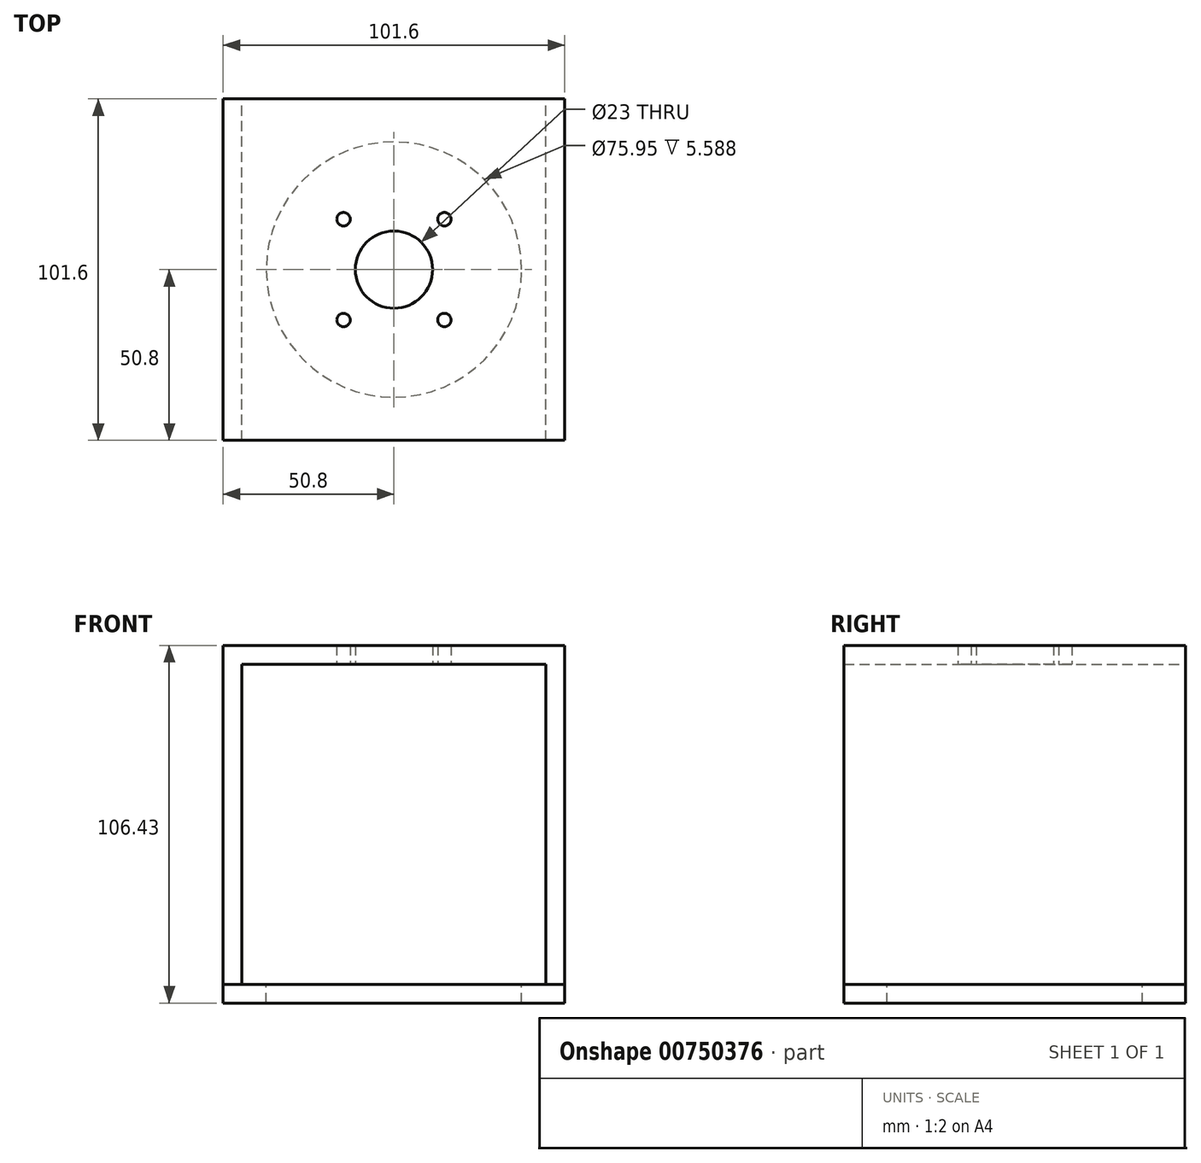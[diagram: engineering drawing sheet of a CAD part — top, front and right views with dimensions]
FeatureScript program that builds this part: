
annotation { "Feature Type Name" : "Feature", "Feature Type Description" : "" }
export const myFeature = defineFeature(function(context is Context, id is Id, definition is map)
    precondition{}
    {
        {
            var Q0;
            Q0=qCreatedBy(makeId("Top.planeOp"),FACE);
            var sketch = newSketch(context, id + "F0", { "sketchPlane" : qUnion([Q0])});
            skLineSegment(sketch, "E0.bottom", {"start": v(50.8, -50.8) * mm, "end": v(-50.8, -50.8) * mm});
            skLineSegment(sketch, "E0.top", {"start": v(50.8, 50.8) * mm, "end": v(-50.8, 50.8) * mm});
            skLineSegment(sketch, "E0.left", {"start": v(50.8, -50.8) * mm, "end": v(50.8, 50.8) * mm});
            skLineSegment(sketch, "E0.right", {"start": v(-50.8, -50.8) * mm, "end": v(-50.8, 50.8) * mm});
            skPoint(sketch, "E0.middle", {"position": v(0, 0) * mm});
            skCircle(sketch, "E1", {"center": v(0, 0) * mm, "radius": 11.5 * mm});
            skCircle(sketch, "E2", {"center": v(-15, 15) * mm, "radius": 2 * mm});
            skCircle(sketch, "E3", {"center": v(15, 15) * mm, "radius": 2 * mm});
            skCircle(sketch, "E4", {"center": v(15, -15) * mm, "radius": 2 * mm});
            skCircle(sketch, "E5", {"center": v(-15, -15) * mm, "radius": 2 * mm});
            skSolve(sketch);
        }
        {
            var Q0;
            Q0=makeQuery(id+"F0.imprint","IMPRINT",FACE,{"disambiguationData":[TD([[makeQuery(id+"F0.imprint","IMPRINT",EDGE,{"derivedFrom":sQuery(id+"F0.wireOp",EDGE,"E0.bottom")}),-1.0]])]});
            extrude(context, id + "F1", {"entities" : qUnion([Q0]), "depth" : 5.6 * mm, "offsetDistance" : 25.4 * mm});
        }
        {
            var Q0;
            Q0=makeQuery(id+"F1.opExtrude","SWEPT_FACE",FACE,{"disambiguationData":[OSD([sQuery(id+"F0.wireOp",EDGE,"E0.left")])]});
            var sketch = newSketch(context, id + "F2", { "sketchPlane" : qUnion([Q0])});
            skLineSegment(sketch, "E6.bottom", {"start": v(-50.8, 0) * mm, "end": v(50.8, 0) * mm});
            skLineSegment(sketch, "E6.top", {"start": v(-50.8, -95.25) * mm, "end": v(50.8, -95.25) * mm});
            skLineSegment(sketch, "E6.left", {"start": v(-50.8, 0) * mm, "end": v(-50.8, -95.25) * mm});
            skLineSegment(sketch, "E6.right", {"start": v(50.8, 0) * mm, "end": v(50.8, -95.25) * mm});
            skSolve(sketch);
        }
        {
            var Q0;
            Q0=makeQuery(id+"F2.imprint","IMPRINT",FACE,{"disambiguationData":[TD([[makeQuery(id+"F2.imprint","IMPRINT",EDGE,{"derivedFrom":sQuery(id+"F2.wireOp",EDGE,"E6.bottom")}),-1.0]])]});
            extrude(context, id + "F3", {"entities" : qUnion([Q0]), "oppositeDirection" : true, "depth" : 5.6 * mm, "offsetDistance" : 25.4 * mm});
        }
        {
            var Q0;
            Q0=makeQuery(id+"F3.opExtrude","SWEPT_BODY",BODY,{"disambiguationData":[OSD([sQuery(id+"F2.wireOp",EDGE,"E6.bottom"),sQuery(id+"F2.wireOp",EDGE,"E6.top"),sQuery(id+"F2.wireOp",EDGE,"E6.left"),sQuery(id+"F2.wireOp",EDGE,"E6.right")])]});
            var Q1;
            Q1=qCreatedBy(makeId("Right.planeOp"),FACE);
            mirror(context, id + "F4", {"operationType" : NewBodyOperationType.ADD, "entities" : qUnion([Q0]), "mirrorPlane" : qUnion([Q1])});
        }
        {
            var Q0;
            Q0=makeQuery(id+"F4.opPattern","COPY",FACE,{"derivedFrom":makeQuery(id+"F3.opExtrude","SWEPT_FACE",FACE,{"disambiguationData":[OSD([sQuery(id+"F2.wireOp",EDGE,"E6.top")])]}),"instanceName":"1"});
            var sketch = newSketch(context, id + "F5", { "sketchPlane" : qUnion([Q0])});
            skLineSegment(sketch, "E7.bottom", {"start": v(-50.8, 50.8) * mm, "end": v(50.8, 50.8) * mm});
            skLineSegment(sketch, "E7.top", {"start": v(-50.8, -50.8) * mm, "end": v(50.8, -50.8) * mm});
            skLineSegment(sketch, "E7.left", {"start": v(-50.8, 50.8) * mm, "end": v(-50.8, -50.8) * mm});
            skLineSegment(sketch, "E7.right", {"start": v(50.8, 50.8) * mm, "end": v(50.8, -50.8) * mm});
            skCircle(sketch, "E8", {"center": v(0, 0) * mm, "radius": 37.97 * mm});
            skSolve(sketch);
        }
        {
            var Q0;
            Q0 = qSketchRegion(id + "F5", true);
            extrude(context, id + "F6", {"entities" : qUnion([Q0]), "depth" : 5.6 * mm, "offsetDistance" : 25.4 * mm});
        }
    });
